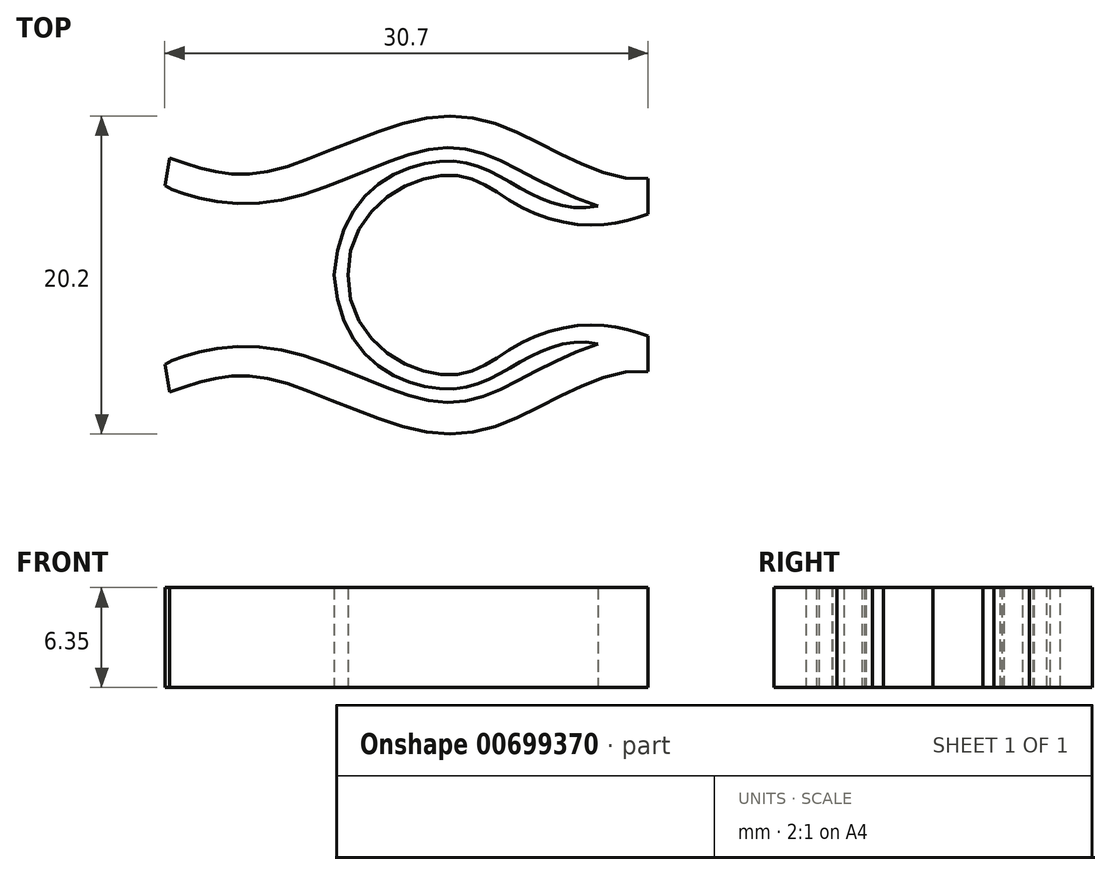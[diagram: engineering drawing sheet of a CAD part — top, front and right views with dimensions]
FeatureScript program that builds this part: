
annotation { "Feature Type Name" : "Feature", "Feature Type Description" : "" }
export const myFeature = defineFeature(function(context is Context, id is Id, definition is map)
    precondition{}
    {
        {
            var Q0;
            Q0=qCreatedBy(makeId("Top.planeOp"),FACE);
            var sketch = newSketch(context, id + "F0", { "sketchPlane" : qUnion([Q0])});
            skCircle(sketch, "E0", {"center": v(0, 0) * mm, "radius": 6.35 * mm, "construction": true});
            skCircle(sketch, "E1", {"center": v(0, 0) * mm, "radius": 7.24 * mm, "construction": true});
            skLineSegment(sketch, "E2.bottom", {"start": v(0, 3.17) * mm, "end": v(12.7, 3.17) * mm, "construction": true});
            skLineSegment(sketch, "E2.top", {"start": v(0, 0) * mm, "end": v(12.7, 0) * mm, "construction": true});
            skLineSegment(sketch, "E2.left", {"start": v(0, 3.17) * mm, "end": v(0, 0) * mm, "construction": true});
            skLineSegment(sketch, "E2.right", {"start": v(12.7, 3.17) * mm, "end": v(12.7, 0) * mm, "construction": true});
            skFitSpline(sketch, "E3", {"points": [v(-6.35, 0) * mm, v(0, 6.35) * mm, v(4.7, 4.28) * mm, v(9.51, 3.17) * mm, v(12.7, 3.87) * mm], "startDerivative": vector(-0.97, 38.29) * mm, "endDerivative": vector(15.58, 4.6) * mm});
            skFitSpline(sketch, "E4", {"points": [v(-7.24, 0) * mm, v(0, 7.24) * mm, v(4.86, 5.37) * mm, v(9.52, 4.37) * mm], "startDerivative": vector(1.78, 38.42) * mm, "endDerivative": vector(18.1, 3.78) * mm});
            skFitSpline(sketch, "E5", {"points": [v(9.52, 4.37) * mm, v(0, 8.09) * mm, v(-11.37, 4.63) * mm, v(-18, 5.67) * mm], "startDerivative": vector(-33.93, 10.76) * mm, "endDerivative": vector(-6.4, 4.66) * mm});
            skFitSpline(sketch, "E6", {"points": [v(12.7, 6.12) * mm, v(0.99, 10.06) * mm, v(-11.48, 6.56) * mm, v(-17.7, 7.42) * mm], "startDerivative": vector(-33.47, -2.36) * mm, "endDerivative": vector(-22.13, 7.26) * mm});
            skLineSegment(sketch, "E7", {"start": v(-17.7, 7.42) * mm, "end": v(-18, 5.67) * mm});
            skLineSegment(sketch, "E8", {"start": v(12.7, 3.87) * mm, "end": v(12.7, 6.12) * mm});
            skLineSegment(sketch, "E9", {"start": v(-7.24, 0) * mm, "end": v(-6.35, 0) * mm});
            skSolve(sketch);
        }
        {
            var Q0;
            Q0 = qSketchRegion(id + "F0", true);
            extrude(context, id + "F1", {"entities" : qUnion([Q0]), "depth" : 6.35 * mm, "offsetDistance" : 25.4 * mm});
        }
        {
            var Q0;
            Q0=makeQuery(id+"F1.opExtrude","SWEPT_BODY",BODY,{"disambiguationData":[OSD([sQuery(id+"F0.wireOp",EDGE,"E3"),sQuery(id+"F0.wireOp",EDGE,"E4"),sQuery(id+"F0.wireOp",EDGE,"E5"),sQuery(id+"F0.wireOp",EDGE,"E6"),sQuery(id+"F0.wireOp",EDGE,"E7"),sQuery(id+"F0.wireOp",EDGE,"E8"),sQuery(id+"F0.wireOp",EDGE,"E9")])]});
            var Q1;
            Q1=qCreatedBy(makeId("Front.planeOp"),FACE);
            mirror(context, id + "F2", {"operationType" : NewBodyOperationType.ADD, "entities" : qUnion([Q0]), "mirrorPlane" : qUnion([Q1])});
        }
    });
